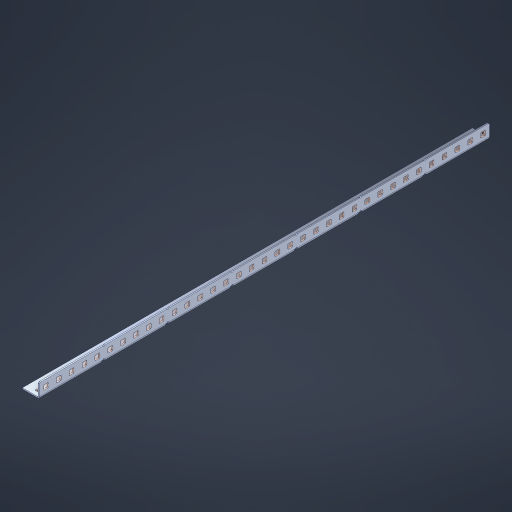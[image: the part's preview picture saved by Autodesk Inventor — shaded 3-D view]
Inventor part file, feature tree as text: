
AUTODESK INVENTOR PART (.ipt)
format: ipt  version: 2023 (Build 270158000, 158)  size: 1,047,552 bytes
history: native  units: in
note: dims shown in document units (in); Inventor stores cm internally (conversion verified against a paired STEP export)
features: other x75, extrude x69, sheet_metal_op x10, sketch x8, mirror x1, pattern_linear x1, chamfer x1
ambient origin geometry x8: Origin, YZ Plane, XZ Plane, XY Plane, X Axis, Y Axis, Z Axis, Center Point
bodies: Solid1 (feature_tree), Body (feature_tree)
feature tree (165):
  other  "Flange Pattern Plane"
  sheet_metal_op  "Flange Pattern"
  sheet_metal_op  "Body Pattern"
  other  "Arc Length"
  mirror  "Notch Mirror"
  pattern_linear  "Notch Pattern"  Spacing1=0.1875in  [1 undecoded]
  chamfer  "End Chamfer"
  extrude  "Half Cut"  Depth=0.0469in
  sketch  "Sketch1"  dims[d0=2.5in]
  other  "Plate1"
  sketch  "Sketch2"  dims[d1=17.5in]
  other  "Plate2"
  sheet_metal_op  "Bend1"
  sheet_metal_op  "Corner1"
  sketch  "Sketch3"  dims[d2=0.0469in]
  other  "Flange Pattern Sketch"
  sketch  "Sketch7"  dims[d3=0.0469in]
  other  "Srf1"
  other  "Srf2"
  sketch  "Sketch8"  dims[d4=0.0234in]
  sketch  "Sketch9"  dims[d5=0.0938in]
  other  "Srf91"
  sheet_metal_op  "Body Pattern Sketch"
  other  "Srf92"
  sketch  "Sketch13"  dims[d6=0.0469in]
  sketch  "Sketch14"  dims[d7=0.5in d8=90.0deg d9=0.0312in d10=0.1875in d11=0.0469in d12=0.0469in d16=0.182in d17=0.02in d18=0.0469in d19=0.0in d20=0.25in d21=0.25in d46=0.172in d47=1.0in d48=0.0in d49=0.182in d50=0.02in d51=0.25in d52=0.25in d53=0.0469in d54=0.0in d55=0.172in d56=1.0in d57=0.0in d60=13.7795in d62=0.5in d63=0.3937in d65=0.5in d85=0.1227in d86=0.1659in d88=0.04in d89=0.0469in d90=0.0in d91=0.04in d92=0.0491in d95=2.5in d96=0.04in d97=0.25in d98=45.0deg d101=0.0in d102=2.497in d131=0.5in d132=13.7795in d134=0.5in d139=0.5in]
  other  "Srf856"
  other  "Srf1310"
  other  "Srf1311"
  other  "Srf1312"
  other  "Srf1376"
  other  "Srf1377"
  other  "Srf1728"
  other  "Srf1755"
  other  "Srf1878"
  other  "Srf1879"
  other  "Srf1880"
  other  "Srf1881"
  other  "Srf1882"
  other  "Srf1883"
  other  "Srf1884"
  other  "Srf1885"
  other  "Srf1886"
  other  "Srf1887"
  other  "Srf1888"
  other  "Srf1889"
  other  "Srf1890"
  other  "Srf1891"
  other  "Srf1892"
  other  "Srf1893"
  other  "Srf1894"
  other  "Srf1895"
  other  "Srf1896"
  other  "Srf1897"
  other  "Srf1898"
  other  "Srf1899"
  other  "Srf1900"
  other  "Srf1901"
  other  "Srf1902"
  other  "Srf1903"
  other  "Srf1904"
  other  "Srf1905"
  other  "Srf1906"
  other  "Srf1942"
  other  "Srf1943"
  other  "Srf1944"
  other  "Srf1945"
  other  "Srf1946"
  other  "Srf1947"
  other  "Srf1948"
  other  "Srf1949"
  other  "Srf1950"
  other  "Srf1951"
  other  "Srf1952"
  other  "Srf1953"
  other  "Srf1954"
  other  "Srf1955"
  other  "Srf1956"
  other  "Srf1957"
  other  "Srf1958"
  other  "Srf1959"
  other  "Srf1960"
  other  "Srf1961"
  other  "Srf1962"
  other  "Srf1963"
  other  "Srf1964"
  other  "Srf1965"
  other  "Srf1966"
  other  "Srf1967"
  other  "Srf1968"
  other  "Srf1969"
  other  "Srf1970"
  sheet_metal_op  "Flange Stamp"
  sheet_metal_op  "Flange Circle"
  sheet_metal_op  "Body Stamp"
  sheet_metal_op  "Body Circle"
  sheet_metal_op  "Notch"
  extrude  "ExtrusionSrf2"  Depth=0.0469in
  extrude  "ExtrusionSrf92"  Depth=0.5in
  extrude  "ExtrusionSrf856"  Depth=0.02in
  extrude  "ExtrusionSrf1310"  Depth=0.0469in
  extrude  "ExtrusionSrf1311"  TaperAngle=0.0deg  [1 undecoded]
  extrude  "ExtrusionSrf1312"  Depth=0.5in
  extrude  "ExtrusionSrf1376"  Depth=0.5in
  extrude  "ExtrusionSrf1377"  Depth=0.5in
  extrude  "ExtrusionSrf1728"  Depth=0.5in TaperAngle=0.0deg
  extrude  "ExtrusionSrf1755"  Depth=0.5in
  extrude  "ExtrusionSrf1878"  Depth=0.02in
  extrude  "ExtrusionSrf1879"  Depth=0.5in
  extrude  "ExtrusionSrf1880"  Depth=0.5in
  extrude  "ExtrusionSrf1881"  Depth=0.0469in
  extrude  "ExtrusionSrf1882"  TaperAngle=0.0deg  [1 undecoded]
  extrude  "ExtrusionSrf1883"  Depth=0.5in
  extrude  "ExtrusionSrf1884"  Depth=0.5in TaperAngle=0.0deg
  extrude  "ExtrusionSrf1885"  Depth=0.5in
  extrude  "ExtrusionSrf1886"  Depth=0.5in
  extrude  "ExtrusionSrf1887"  Depth=0.5in
  extrude  "ExtrusionSrf1888"  Depth=0.5in
  extrude  "ExtrusionSrf1889"  Depth=0.5in
  extrude  "ExtrusionSrf1890"  Depth=0.0469in
  extrude  "ExtrusionSrf1891"  TaperAngle=0.0deg  [1 undecoded]
  extrude  "ExtrusionSrf1892"  Depth=0.5in
  extrude  "ExtrusionSrf1893"  Depth=0.5in
  extrude  "ExtrusionSrf1894"  Depth=0.5in
  extrude  "ExtrusionSrf1895"  Depth=0.5in TaperAngle=45.0deg
  extrude  "ExtrusionSrf1896"  TaperAngle=0.0deg  [1 undecoded]
  extrude  "ExtrusionSrf1897"  Depth=0.5in
  extrude  "ExtrusionSrf1898"  Depth=0.5in
  extrude  "ExtrusionSrf1899"  Depth=0.5in
  extrude  "ExtrusionSrf1900"  Depth=0.5in
  extrude  "ExtrusionSrf1901"  Depth=0.5in
  extrude  "ExtrusionSrf1902"  [1 undecoded]
  extrude  "ExtrusionSrf1903"  [1 undecoded]
  extrude  "ExtrusionSrf1904"  [1 undecoded]
  extrude  "ExtrusionSrf1905"  [1 undecoded]
  extrude  "ExtrusionSrf1906"  [1 undecoded]
  extrude  "ExtrusionSrf1942"  [1 undecoded]
  extrude  "ExtrusionSrf1943"  [1 undecoded]
  extrude  "ExtrusionSrf1944"  [1 undecoded]
  extrude  "ExtrusionSrf1945"  [1 undecoded]
  extrude  "ExtrusionSrf1946"  [1 undecoded]
  extrude  "ExtrusionSrf1947"  [1 undecoded]
  extrude  "ExtrusionSrf1948"  [1 undecoded]
  extrude  "ExtrusionSrf1949"  [1 undecoded]
  extrude  "ExtrusionSrf1950"  [1 undecoded]
  extrude  "ExtrusionSrf1951"  [1 undecoded]
  extrude  "ExtrusionSrf1952"  [1 undecoded]
  extrude  "ExtrusionSrf1953"  [1 undecoded]
  extrude  "ExtrusionSrf1954"  [1 undecoded]
  extrude  "ExtrusionSrf1955"  [1 undecoded]
  extrude  "ExtrusionSrf1956"  [1 undecoded]
  extrude  "ExtrusionSrf1957"  [1 undecoded]
  extrude  "ExtrusionSrf1958"  [1 undecoded]
  extrude  "ExtrusionSrf1959"  [1 undecoded]
  extrude  "ExtrusionSrf1960"  [1 undecoded]
  extrude  "ExtrusionSrf1961"  [1 undecoded]
  extrude  "ExtrusionSrf1962"  [1 undecoded]
  extrude  "ExtrusionSrf1963"  [1 undecoded]
  extrude  "ExtrusionSrf1964"  [1 undecoded]
  extrude  "ExtrusionSrf1965"  [1 undecoded]
  extrude  "ExtrusionSrf1966"  [1 undecoded]
  extrude  "ExtrusionSrf1967"  [1 undecoded]
  extrude  "ExtrusionSrf1968"  [1 undecoded]
  extrude  "ExtrusionSrf1969"  [1 undecoded]
  extrude  "ExtrusionSrf1970"  [1 undecoded]
note: 39 required parameter values undecoded (feature->parameter linkage not recoverable at this tier; creation-order binding heuristic only, values carry confidence <= 0.55)
